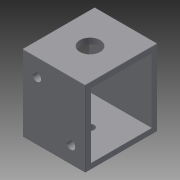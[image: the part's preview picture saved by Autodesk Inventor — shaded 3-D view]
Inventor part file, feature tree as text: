
AUTODESK INVENTOR PART (.ipt)
format: ipt  version: 2015 (Build 190159000, 159)  size: 132,608 bytes
history: native  units: mm
features: extrude x4, sketch x4, shell x1, fillet x1
ambient origin geometry x8: Origin, YZ Plane, XZ Plane, XY Plane, X Axis, Y Axis, Z Axis, Center Point
bodies: Solid1 (feature_tree)
feature tree (10):
  extrude  "Extrusion1"  Depth=26.8mm
  shell  "Shell1"  Thickness=25.4mm
  extrude  "Extrusion2"  Depth=3.0mm
  extrude  "Extrusion3"  Depth=6.0mm
  extrude  "Extrusion4"  Depth=25.4mm TaperAngle=0.0deg
  fillet  "Fillet1"  Radius=2.0mm
  sketch  "Sketch1"  dims[d0=22.1mm d1=26.8mm d2=25.4mm d3=0.0mm]
  sketch  "Sketch2"  dims[d4=19.0mm d5=3.0mm]
  sketch  "Sketch3"  dims[d6=3.0mm d7=6.0mm]
  sketch  "Sketch4"  dims[d8=12.0mm d9=25.4mm d10=0.0mm d11=2.0mm d12=7.2mm d13=25.4mm d14=0.0mm d15=3.0mm d16=25.4mm d17=0.0mm d18=0.2mm]
